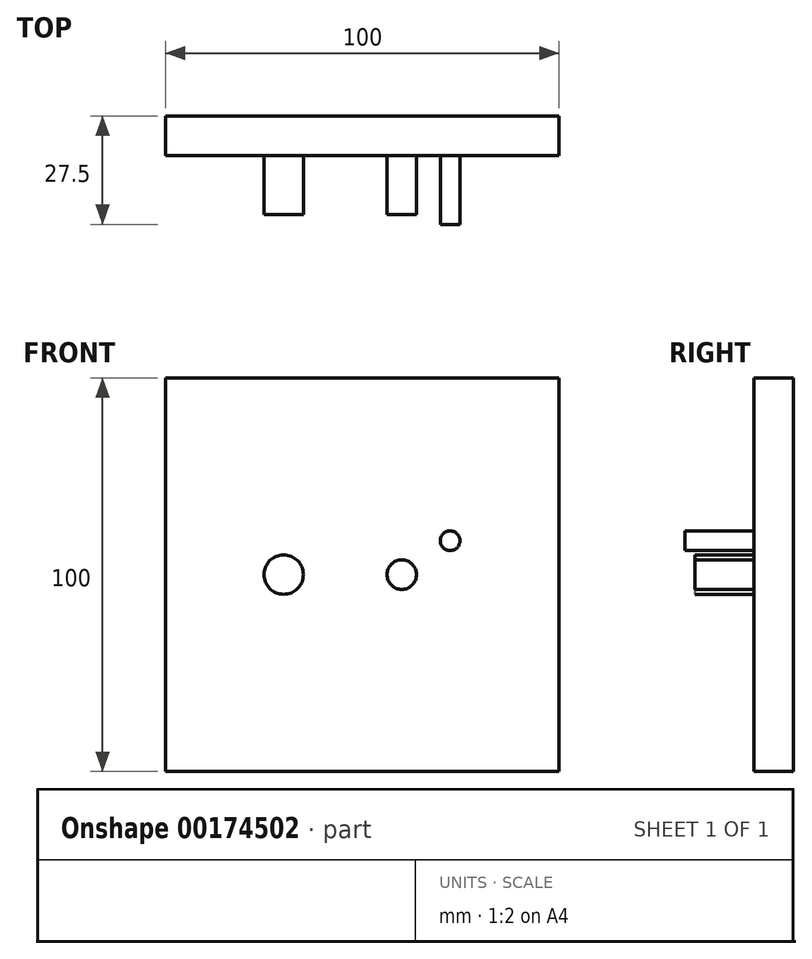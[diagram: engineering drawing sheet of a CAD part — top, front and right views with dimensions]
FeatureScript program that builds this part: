
annotation { "Feature Type Name" : "Feature", "Feature Type Description" : "" }
export const myFeature = defineFeature(function(context is Context, id is Id, definition is map)
    precondition{}
    {
        {
            var Q0;
            Q0=qCreatedBy(makeId("Front.planeOp"),FACE);
            var sketch = newSketch(context, id + "F0", { "sketchPlane" : qUnion([Q0])});
            skLineSegment(sketch, "E0.bottom", {"start": v(50, -50) * mm, "end": v(-50, -50) * mm});
            skLineSegment(sketch, "E0.top", {"start": v(50, 50) * mm, "end": v(-50, 50) * mm});
            skLineSegment(sketch, "E0.left", {"start": v(50, -50) * mm, "end": v(50, 50) * mm});
            skLineSegment(sketch, "E0.right", {"start": v(-50, -50) * mm, "end": v(-50, 50) * mm});
            skPoint(sketch, "E0.middle", {"position": v(0, 0) * mm});
            skSolve(sketch);
        }
        {
            var Q0;
            Q0=makeQuery(id+"F0.imprint","IMPRINT",FACE,{"disambiguationData":[TD([[makeQuery(id+"F0.imprint","IMPRINT",EDGE,{"derivedFrom":sQuery(id+"F0.wireOp",EDGE,"E0.bottom")}),-1.0]])]});
            extrude(context, id + "F1", {"entities" : qUnion([Q0]), "oppositeDirection" : true, "depth" : 10 * mm});
        }
        {
            var Q0;
            Q0=makeQuery(id+"F1.opExtrude","CAP_FACE",FACE,{"disambiguationData":[OSD([sQuery(id+"F0.wireOp",EDGE,"E0.bottom"),sQuery(id+"F0.wireOp",EDGE,"E0.top"),sQuery(id+"F0.wireOp",EDGE,"E0.left"),sQuery(id+"F0.wireOp",EDGE,"E0.right")])],"isStart":true});
            var sketch = newSketch(context, id + "F2", { "sketchPlane" : qUnion([Q0])});
            skLineSegment(sketch, "E1", {"start": v(-20, 0) * mm, "end": v(10, 0) * mm});
            skCircle(sketch, "E2", {"center": v(10, 0) * mm, "radius": 3.75 * mm});
            skCircle(sketch, "E3", {"center": v(-20, 0) * mm, "radius": 5 * mm});
            skLineSegment(sketch, "E4", {"start": v(10, 0) * mm, "end": v(22.29, 8.6) * mm});
            skCircle(sketch, "E5", {"center": v(22.29, 8.6) * mm, "radius": 2.5 * mm});
            skSolve(sketch);
        }
        {
            var Q0;
            Q0=makeQuery(id+"F2.imprint","IMPRINT",FACE,{"disambiguationData":[TD([[makeQuery(id+"F2.imprint","IMPRINT",EDGE,{"derivedFrom":sQuery(id+"F2.wireOp",EDGE,"E3")}),1.0]])]});
            var Q1;
            {var subQ0=sQuery(id+"F2.wireOp",EDGE,"E4");var subQ1=sQuery(id+"F2.wireOp",EDGE,"E1");var subQ2=makeQuery(id+"F2.imprint","INTERSECT",VERTEX,{"derivedFrom":[subQ1,subQ0]});Q1=makeQuery(id+"F2.imprint","IMPRINT",FACE,{"disambiguationData":[TD([[makeQuery(id+"F2.imprint","IMPRINT",EDGE,{"disambiguationData":[TD([[subQ2,1.0]])],"derivedFrom":subQ1}),1.0]])]});}
            var Q2;
            {var subQ0=sQuery(id+"F2.wireOp",EDGE,"E4");var subQ1=sQuery(id+"F2.wireOp",EDGE,"E1");var subQ2=makeQuery(id+"F2.imprint","INTERSECT",VERTEX,{"derivedFrom":[subQ1,subQ0]});Q2=makeQuery(id+"F2.imprint","IMPRINT",FACE,{"disambiguationData":[TD([[makeQuery(id+"F2.imprint","IMPRINT",EDGE,{"disambiguationData":[TD([[subQ2,1.0]])],"derivedFrom":subQ1}),-1.0]])]});}
            extrude(context, id + "F3", {"entities" : qUnion([Q0, Q1, Q2]), "operationType" : NewBodyOperationType.ADD, "depth" : 15 * mm});
        }
        {
            var Q0;
            Q0=makeQuery(id+"F2.imprint","IMPRINT",FACE,{"disambiguationData":[TD([[makeQuery(id+"F2.imprint","IMPRINT",EDGE,{"derivedFrom":sQuery(id+"F2.wireOp",EDGE,"E5")}),1.0]])]});
            extrude(context, id + "F4", {"entities" : qUnion([Q0]), "operationType" : NewBodyOperationType.ADD, "depth" : 17.5 * mm});
        }
    });
